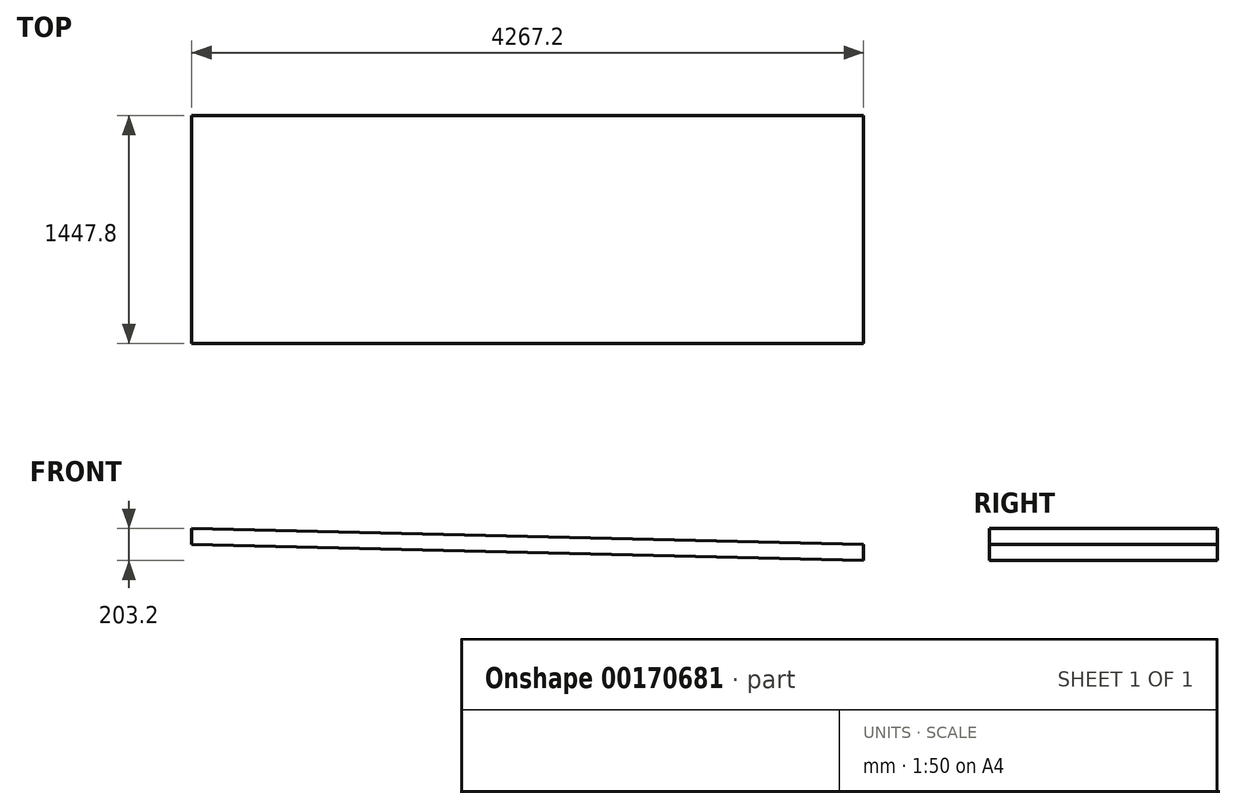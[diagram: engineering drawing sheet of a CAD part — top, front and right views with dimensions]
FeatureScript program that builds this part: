
annotation { "Feature Type Name" : "Feature", "Feature Type Description" : "" }
export const myFeature = defineFeature(function(context is Context, id is Id, definition is map)
    precondition{}
    {
        {
            var Q0;
            Q0=qCreatedBy(makeId("Front.planeOp"),FACE);
            var sketch = newSketch(context, id + "F0", { "sketchPlane" : qUnion([Q0])});
            skLineSegment(sketch, "E0", {"start": v(0, 0) * mm, "end": v(0, 101.6) * mm});
            skLineSegment(sketch, "E1", {"start": v(0, 101.6) * mm, "end": v(4267.2, 0) * mm});
            skLineSegment(sketch, "E2", {"start": v(4267.2, 0) * mm, "end": v(4267.2, -101.6) * mm});
            skLineSegment(sketch, "E3", {"start": v(4267.2, -101.6) * mm, "end": v(0, 0) * mm});
            skSolve(sketch);
        }
        {
            var Q0;
            Q0=makeQuery(id+"F0.imprint","IMPRINT",FACE,{"disambiguationData":[TD([[makeQuery(id+"F0.imprint","IMPRINT",EDGE,{"derivedFrom":sQuery(id+"F0.wireOp",EDGE,"E0")}),-1.0]])]});
            extrude(context, id + "F1", {"entities" : qUnion([Q0]), "depth" : 1447.8 * mm});
        }
    });
